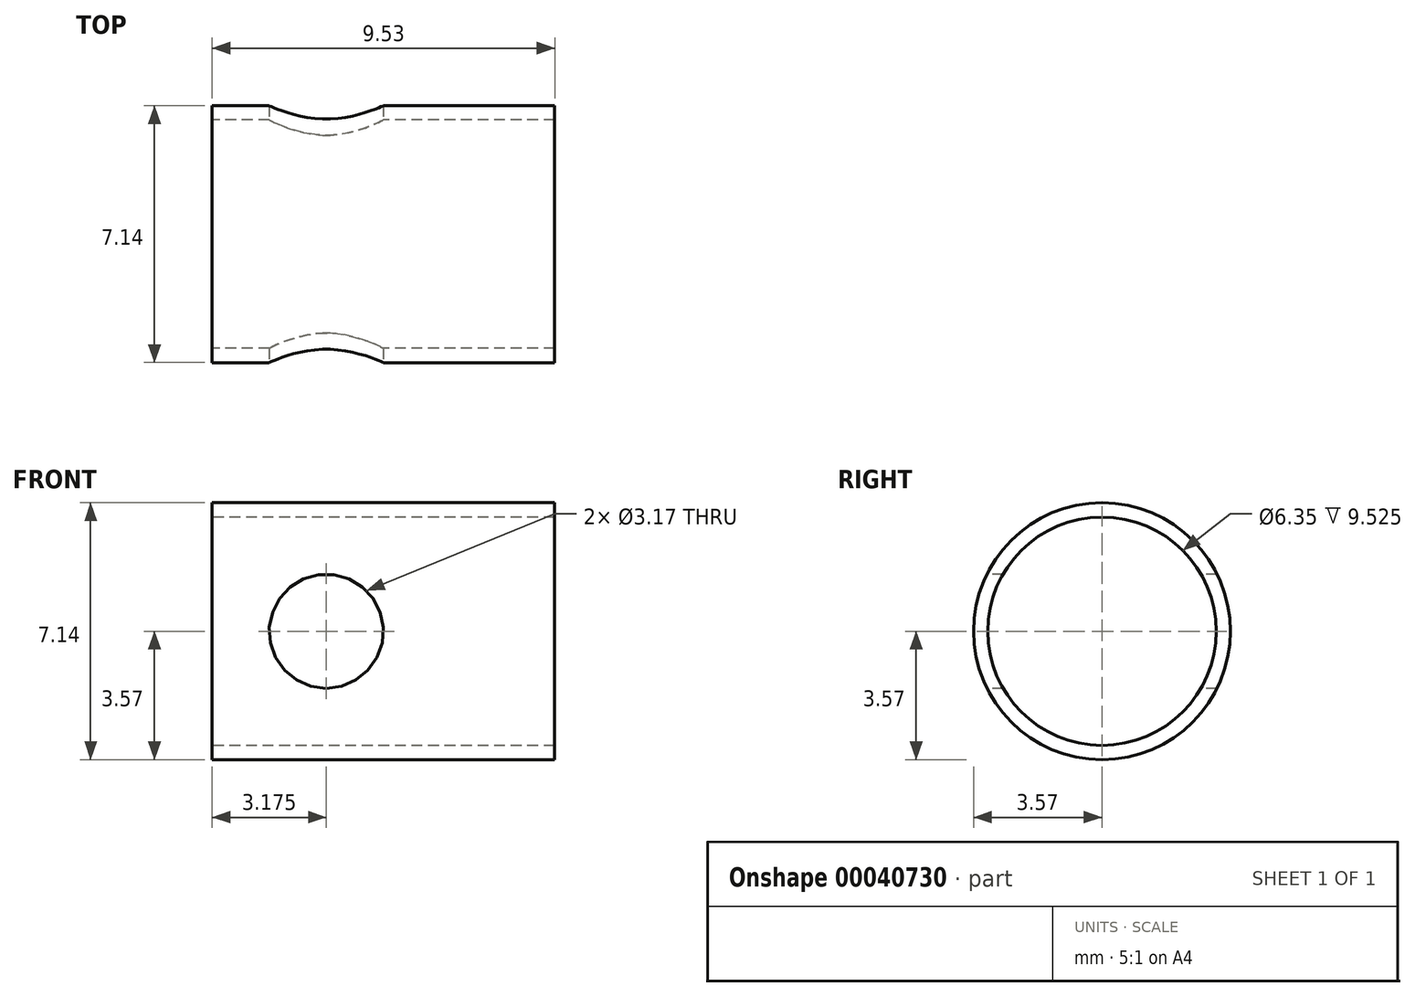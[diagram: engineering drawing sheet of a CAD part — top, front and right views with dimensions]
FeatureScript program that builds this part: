
annotation { "Feature Type Name" : "Feature", "Feature Type Description" : "" }
export const myFeature = defineFeature(function(context is Context, id is Id, definition is map)
    precondition{}
    {
        {
            var Q0;
            Q0=qCreatedBy(makeId("Right.planeOp"),FACE);
            var sketch = newSketch(context, id + "F0", { "sketchPlane" : qUnion([Q0])});
            skCircle(sketch, "E0", {"center": v(0, 0) * mm, "radius": 3.57 * mm});
            skCircle(sketch, "E1", {"center": v(0, 0) * mm, "radius": 3.18 * mm});
            skSolve(sketch);
        }
        {
            var Q0;
            Q0 = qSketchRegion(id + "F0", true);
            var Q1;
            Q1=sQuery(id+"F0.wireOp",EDGE,"E1");
            var Q2;
            Q2=sQuery(id+"F0.wireOp",EDGE,"E0");
            extrude(context, id + "F1", {"entities" : qUnion([Q0]), "surfaceEntities" : qUnion([Q1, Q2]), "depth" : 9.52 * mm});
        }
        {
            var Q0;
            Q0=qCreatedBy(makeId("Front.planeOp"),FACE);
            var sketch = newSketch(context, id + "F2", { "sketchPlane" : qUnion([Q0])});
            skCircle(sketch, "E2", {"center": v(3.18, 0) * mm, "radius": 1.59 * mm});
            skSolve(sketch);
        }
        {
            var Q0;
            Q0 = qSketchRegion(id + "F2", true);
            extrude(context, id + "F3", {"entities" : qUnion([Q0]), "operationType" : NewBodyOperationType.REMOVE, "endBound" : BoundingType.SYMMETRIC, "oppositeDirection" : true, "depth" : 25.4 * mm});
        }
    });
